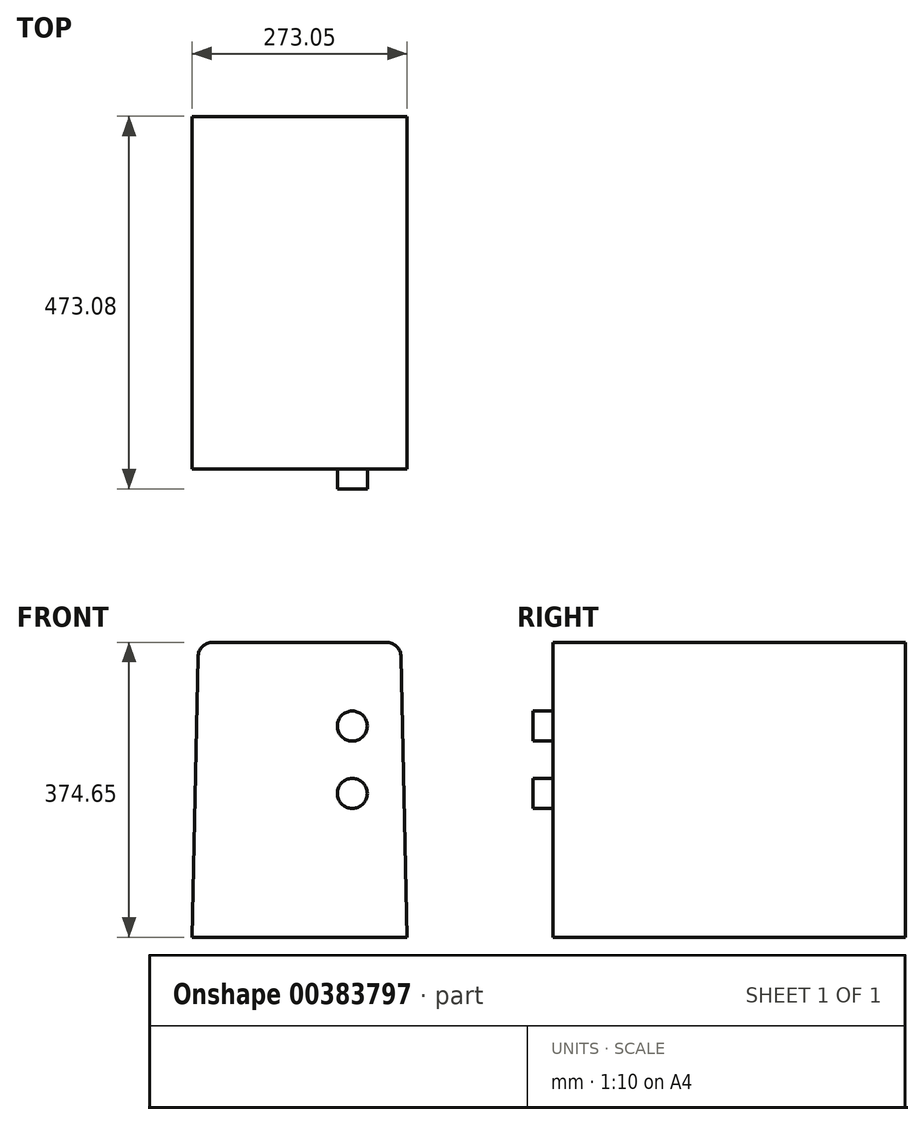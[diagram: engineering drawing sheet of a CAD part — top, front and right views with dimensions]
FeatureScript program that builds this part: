
annotation { "Feature Type Name" : "Feature", "Feature Type Description" : "" }
export const myFeature = defineFeature(function(context is Context, id is Id, definition is map)
    precondition{}
    {
        {
            var Q0;
            Q0=qCreatedBy(makeId("Front.planeOp"),FACE);
            var sketch = newSketch(context, id + "F0", { "sketchPlane" : qUnion([Q0])});
            skLineSegment(sketch, "E0", {"start": v(3.12, 185.43) * mm, "end": v(113.06, 185.43) * mm});
            skLineSegment(sketch, "E1", {"start": v(132.1, 166.78) * mm, "end": v(139.65, -189.22) * mm});
            skLineSegment(sketch, "E2", {"start": v(139.65, -189.22) * mm, "end": v(3.12, -189.22) * mm});
            skLineSegment(sketch, "E3", {"start": v(3.12, 185.43) * mm, "end": v(3.12, -189.22) * mm, "construction": true});
            skPoint(sketch, "E4.end.orphan", {"position": v(-125.47, 185.43) * mm});
            skPoint(sketch, "E5.orphan", {"position": v(-133.4, -189.22) * mm});
            skLineSegment(sketch, "E6.MirrorCS", {"start": v(3.12, 185.43) * mm, "end": v(-106.82, 185.43) * mm});
            skLineSegment(sketch, "E7.MirrorCS", {"start": v(-125.86, 166.78) * mm, "end": v(-133.4, -189.22) * mm});
            skLineSegment(sketch, "E8.MirrorCS", {"start": v(-133.4, -189.22) * mm, "end": v(3.12, -189.22) * mm});
            skArc(sketch, "E9.filletArc", {"start": v(-106.82, 185.43) * mm, "mid": v(-120.14, 180) * mm, "end": v(-125.86, 166.78) * mm});
            skPoint(sketch, "E10.visualSharp", {"position": v(131.7, 185.43) * mm});
            skArc(sketch, "E10.filletArc", {"start": v(132.1, 166.78) * mm, "mid": v(126.38, 180) * mm, "end": v(113.06, 185.43) * mm});
            skSolve(sketch);
        }
        {
            var Q0;
            Q0 = qSketchRegion(id + "F0", true);
            extrude(context, id + "F1", {"entities" : qUnion([Q0]), "oppositeDirection" : true, "depth" : 447.67 * mm});
        }
        {
            var Q0;
            Q0=makeQuery(id+"F1.opExtrude","CAP_FACE",FACE,{"disambiguationData":[OSD([sQuery(id+"F0.wireOp",EDGE,"E0"),sQuery(id+"F0.wireOp",EDGE,"E1"),sQuery(id+"F0.wireOp",EDGE,"E2"),sQuery(id+"F0.wireOp",EDGE,"E6.MirrorCS"),sQuery(id+"F0.wireOp",EDGE,"E7.MirrorCS"),sQuery(id+"F0.wireOp",EDGE,"E8.MirrorCS")])],"isStart":true});
            var sketch = newSketch(context, id + "F2", { "sketchPlane" : qUnion([Q0])});
            skCircle(sketch, "E11", {"center": v(70.14, 78.94) * mm, "radius": 19.05 * mm});
            skCircle(sketch, "E12", {"center": v(70.14, -6.66) * mm, "radius": 19.05 * mm});
            skSolve(sketch);
        }
        {
            var Q0;
            Q0=makeQuery(id+"F2.imprint","IMPRINT",FACE,{"disambiguationData":[TD([[makeQuery(id+"F2.imprint","IMPRINT",EDGE,{"derivedFrom":sQuery(id+"F2.wireOp",EDGE,"E11")}),1.0]])]});
            var Q1;
            Q1=makeQuery(id+"F2.imprint","IMPRINT",FACE,{"disambiguationData":[TD([[makeQuery(id+"F2.imprint","IMPRINT",EDGE,{"derivedFrom":sQuery(id+"F2.wireOp",EDGE,"E12")}),1.0]])]});
            extrude(context, id + "F3", {"entities" : qUnion([Q0, Q1]), "operationType" : NewBodyOperationType.ADD, "depth" : 25.4 * mm});
        }
    });
